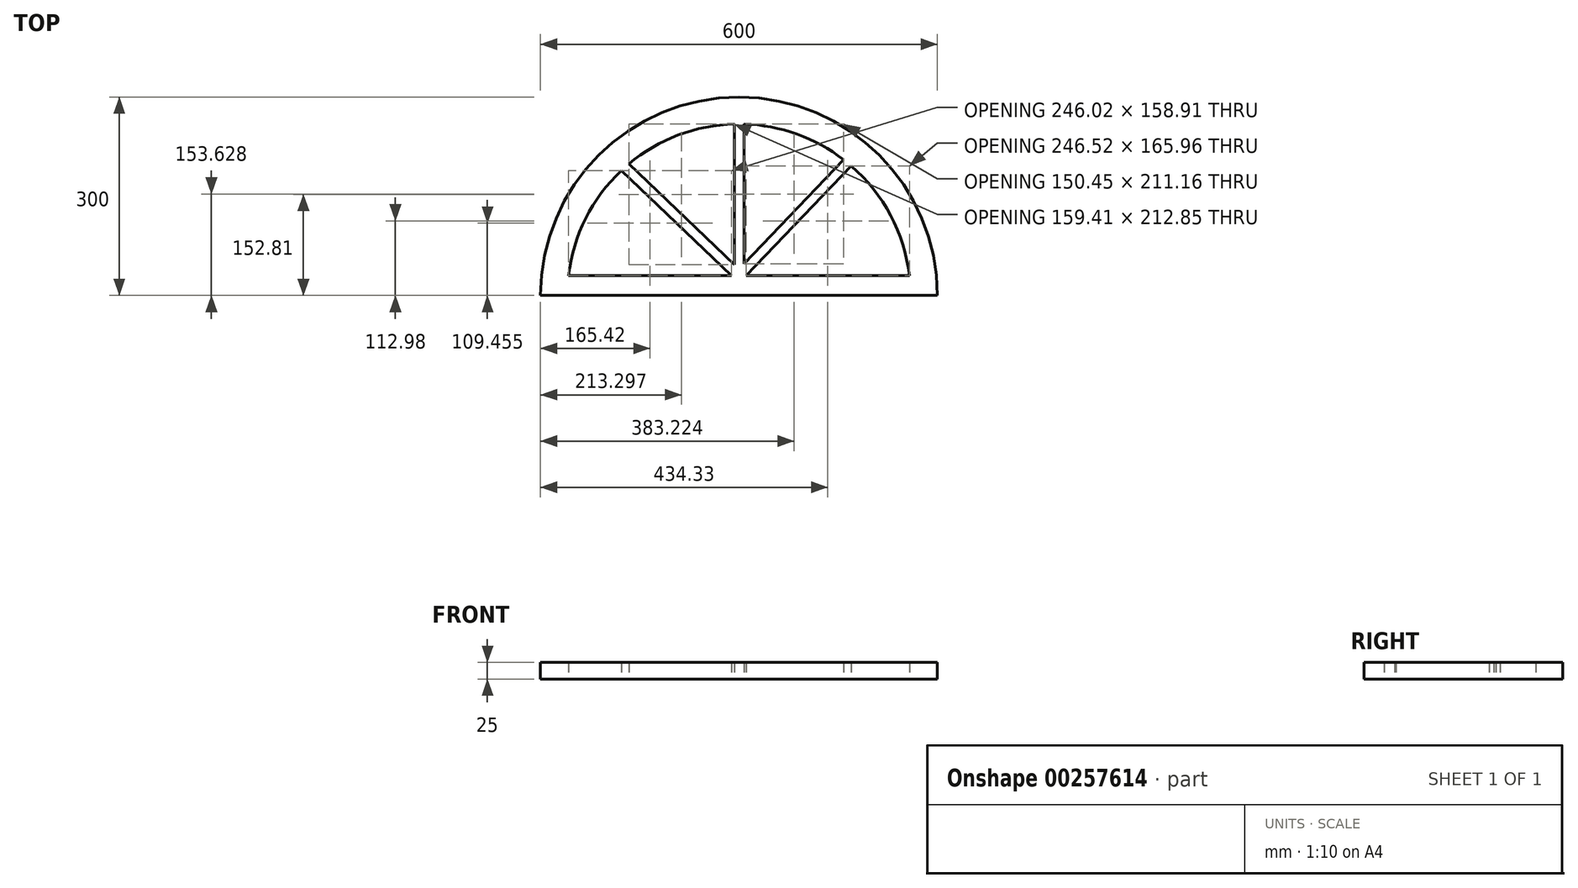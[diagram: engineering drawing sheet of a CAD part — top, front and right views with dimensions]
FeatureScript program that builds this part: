
annotation { "Feature Type Name" : "Feature", "Feature Type Description" : "" }
export const myFeature = defineFeature(function(context is Context, id is Id, definition is map)
    precondition{}
    {
        {
            var Q0;
            Q0=qCreatedBy(makeId("Top.planeOp"),FACE);
            var sketch = newSketch(context, id + "F0", { "sketchPlane" : qUnion([Q0])});
            skArc(sketch, "E0", {"start": v(300, 0) * mm, "mid": v(0, 300) * mm, "end": v(-300, 0) * mm});
            skLineSegment(sketch, "E1", {"start": v(-300, 0) * mm, "end": v(300, 0) * mm});
            skArc(sketch, "E2", {"start": v(257.59, 30) * mm, "mid": v(229.27, 121.2) * mm, "end": v(169.86, 195.96) * mm});
            skLineSegment(sketch, "E3", {"start": v(-257.59, 30) * mm, "end": v(-11.57, 30) * mm});
            skPoint(sketch, "E4.endSnap0", {"position": v(0, 300) * mm});
            skLineSegment(sketch, "E5", {"start": v(-100.46, 135.8) * mm, "end": v(-166.4, 198.9) * mm});
            skLineSegment(sketch, "E6", {"start": v(-166.4, 198.9) * mm, "end": v(-7, 46.39) * mm});
            skLineSegment(sketch, "E7", {"start": v(-110.83, 124.96) * mm, "end": v(-177.66, 188.91) * mm});
            skLineSegment(sketch, "E8", {"start": v(-177.66, 188.91) * mm, "end": v(-11.57, 30) * mm});
            skLineSegment(sketch, "E9", {"start": v(8, 48.05) * mm, "end": v(158.45, 205.3) * mm});
            skLineSegment(sketch, "E10", {"start": v(96.55, 119.34) * mm, "end": v(169.86, 195.96) * mm});
            skLineSegment(sketch, "E11", {"start": v(169.86, 195.96) * mm, "end": v(11.07, 30) * mm});
            skLineSegment(sketch, "E12", {"start": v(-7, 211.88) * mm, "end": v(-7, 259.23) * mm});
            skLineSegment(sketch, "E13", {"start": v(-7, 259.23) * mm, "end": v(-7, 46.39) * mm});
            skLineSegment(sketch, "E14", {"start": v(8, 211.88) * mm, "end": v(8, 259.2) * mm});
            skLineSegment(sketch, "E15", {"start": v(8, 259.2) * mm, "end": v(8, 48.05) * mm});
            skPoint(sketch, "E16.trimOffspring.end.orphan", {"position": v(0, 294.68) * mm});
            skPoint(sketch, "E4.start.orphan", {"position": v(0, 30) * mm});
            skPoint(sketch, "E17.start.orphan", {"position": v(90.77, 124.87) * mm});
            skArc(sketch, "E18.trimOffspring", {"start": v(-177.66, 188.91) * mm, "mid": v(-231.68, 116.52) * mm, "end": v(-257.59, 30) * mm});
            skArc(sketch, "E19.trimOffspring", {"start": v(-7, 259.23) * mm, "mid": v(-91.8, 242.54) * mm, "end": v(-166.4, 198.9) * mm});
            skArc(sketch, "E20.trimOffspring", {"start": v(158.45, 205.3) * mm, "mid": v(87.48, 244.13) * mm, "end": v(8, 259.2) * mm});
            skLineSegment(sketch, "E21.trimOffspring", {"start": v(11.07, 30) * mm, "end": v(257.59, 30) * mm});
            skSolve(sketch);
        }
        {
            var Q0;
            Q0 = qSketchRegion(id + "F0", true);
            extrude(context, id + "F1", {"entities" : qUnion([Q0]), "depth" : 25 * mm});
        }
    });
